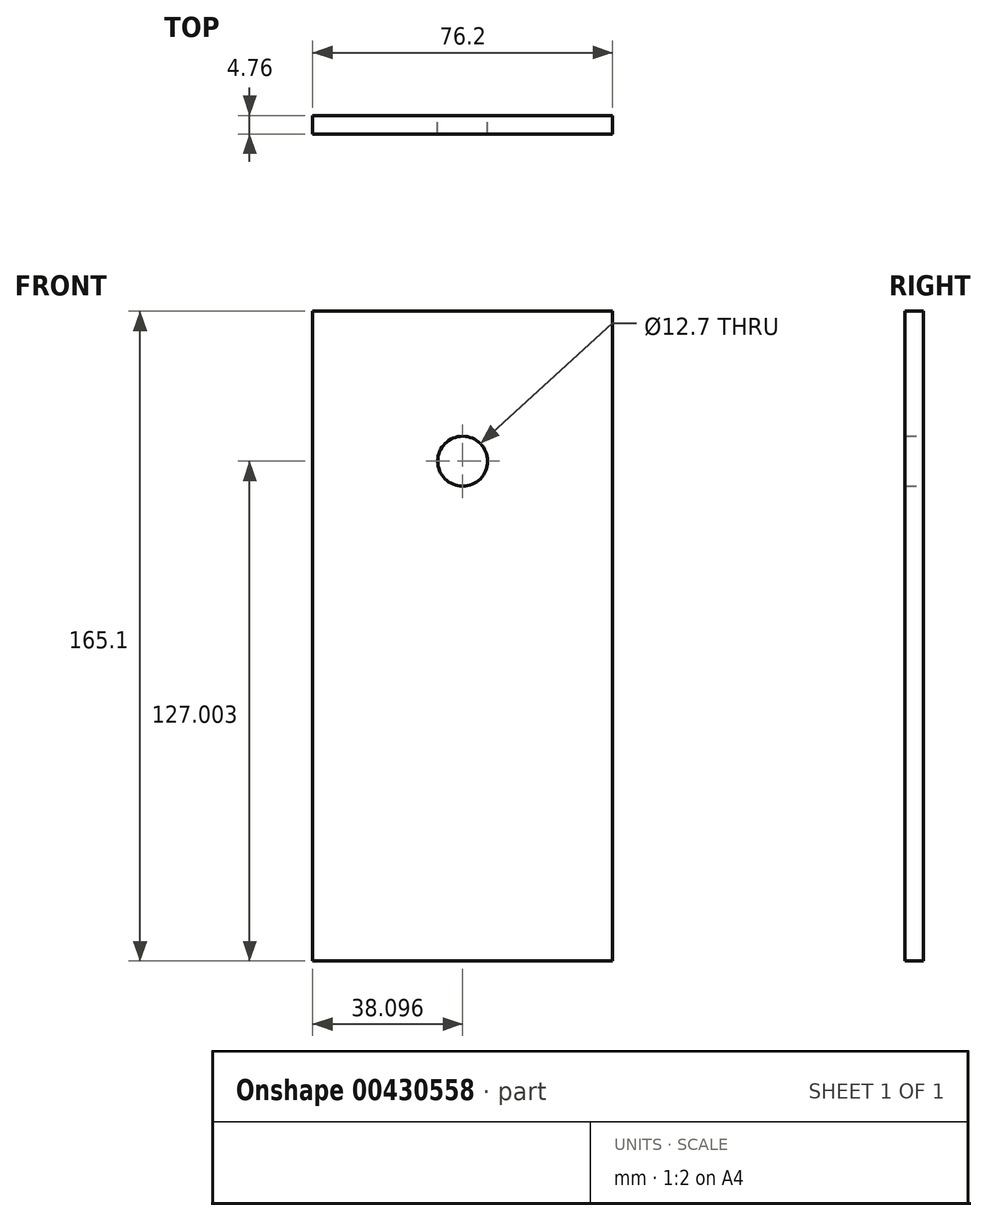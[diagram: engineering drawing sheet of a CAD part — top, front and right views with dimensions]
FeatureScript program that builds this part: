
annotation { "Feature Type Name" : "Feature", "Feature Type Description" : "" }
export const myFeature = defineFeature(function(context is Context, id is Id, definition is map)
    precondition{}
    {
        {
            var Q0;
            Q0=qCreatedBy(makeId("Front.planeOp"),FACE);
            var sketch = newSketch(context, id + "F0", { "sketchPlane" : qUnion([Q0])});
            skLineSegment(sketch, "E0.bottom", {"start": v(-47.77, 108.25) * mm, "end": v(28.43, 108.25) * mm});
            skLineSegment(sketch, "E0.top", {"start": v(-47.77, -56.85) * mm, "end": v(28.43, -56.85) * mm});
            skLineSegment(sketch, "E0.left", {"start": v(-47.77, 108.25) * mm, "end": v(-47.77, -56.85) * mm});
            skLineSegment(sketch, "E0.right", {"start": v(28.43, 108.25) * mm, "end": v(28.43, -56.85) * mm});
            skPoint(sketch, "E1", {"position": v(-9.67, 108.25) * mm});
            skPoint(sketch, "E2", {"position": v(-9.67, 70.15) * mm});
            skCircle(sketch, "E3", {"center": v(-9.67, 70.15) * mm, "radius": 6.35 * mm});
            skSolve(sketch);
        }
        {
            var Q0;
            Q0=makeQuery(id+"F0.imprint","IMPRINT",FACE,{"disambiguationData":[TD([[makeQuery(id+"F0.imprint","IMPRINT",EDGE,{"derivedFrom":sQuery(id+"F0.wireOp",EDGE,"E0.bottom")}),-1.0]])]});
            extrude(context, id + "F1", {"entities" : qUnion([Q0]), "depth" : 4.76 * mm});
        }
    });
